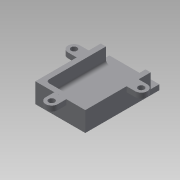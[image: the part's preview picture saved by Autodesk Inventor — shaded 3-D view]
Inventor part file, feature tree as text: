
AUTODESK INVENTOR PART (.ipt)
format: ipt  version: 2015 SP1 (Build 190203100, 203)  size: 244,736 bytes
history: native  units: mm
features: extrude x13, sketch x13, projected_geometry x10, fillet x1
ambient origin geometry x8: Origin, YZ Plane, XZ Plane, XY Plane, X Axis, Y Axis, Z Axis, Center Point
bodies: Solid1 (feature_tree)
feature tree (37):
  extrude  "Extrusion1"  Depth=1.0mm TaperAngle=0.0deg
  sketch  "Sketch2"  dims[d4=1.0mm d5=2.0mm d6=2.0mm]
  extrude  "Extrusion6"  Depth=2.0mm
  fillet  "Fillet1"  Radius=2.0mm
  extrude  "Extrusion8"  Depth=2.0mm
  extrude  "Extrusion9"  Depth=37.0mm
  extrude  "Extrusion10"  Depth=8.5mm TaperAngle=0.0deg
  extrude  "Extrusion11"  Depth=2.0mm TaperAngle=0.0deg
  extrude  "Extrusion12"  Depth=2.0mm TaperAngle=0.0deg
  sketch  "Sketch9"  dims[d63=2.0mm d64=0.0mm d65=4.0mm d66=0.0mm]
  extrude  "Extrusion15"  Depth=2.0mm TaperAngle=0.0deg
  extrude  "Extrusion16"  Depth=11.5mm TaperAngle=0.0deg
  extrude  "Extrusion17"  Depth=3.0mm TaperAngle=0.0deg
  extrude  "Extrusion18"  Depth=2.0mm TaperAngle=0.0deg
  extrude  "Extrusion19"  Depth=2.0mm TaperAngle=0.0deg
  extrude  "Extrusion20"  [1 undecoded]
  sketch  "Sketch1"  dims[d0=25.0mm d2=1.0mm d3=0.0mm]
  sketch  "Sketch4"  dims[d7=2.0mm d8=1.0mm]
  projected_geometry  "Projected Loop2"
  sketch  "Sketch5"  dims[d10=37.0mm d11=37.0mm]
  projected_geometry  "Projected Loop3"
  sketch  "Sketch6"  dims[d12=40.0mm d31=8.5mm d32=0.0mm]
  projected_geometry  "Projected Loop4"
  sketch  "Sketch7"  dims[d33=2.0mm d57=2.0mm d58=0.0mm]
  projected_geometry  "Projected Loop5"
  sketch  "Sketch8"  dims[d59=2.0mm d60=0.0mm d61=2.0mm d62=0.0mm]
  projected_geometry  "Projected Loop6"
  projected_geometry  "Projected Loop7"
  projected_geometry  "Projected Loop8"
  sketch  "Sketch14"  dims[d71=11.0mm d72=0.0mm d73=11.5mm d74=0.0mm]
  sketch  "Sketch16"  dims[d76=3.0mm d77=0.0mm d78=1.0mm d79=0.0mm]
  sketch  "Sketch17"  dims[d80=2.0mm d81=2.0mm d82=0.0mm]
  projected_geometry  "Projected Loop9"
  sketch  "Sketch18"  dims[d83=2.0mm d84=2.0mm d85=0.0mm]
  sketch  "Sketch19"
  projected_geometry  "Projected Loop10"
  projected_geometry  "Projected Loop11"
note: 1 required parameter value undecoded (feature->parameter linkage not recoverable at this tier; creation-order binding heuristic only, values carry confidence <= 0.55)
